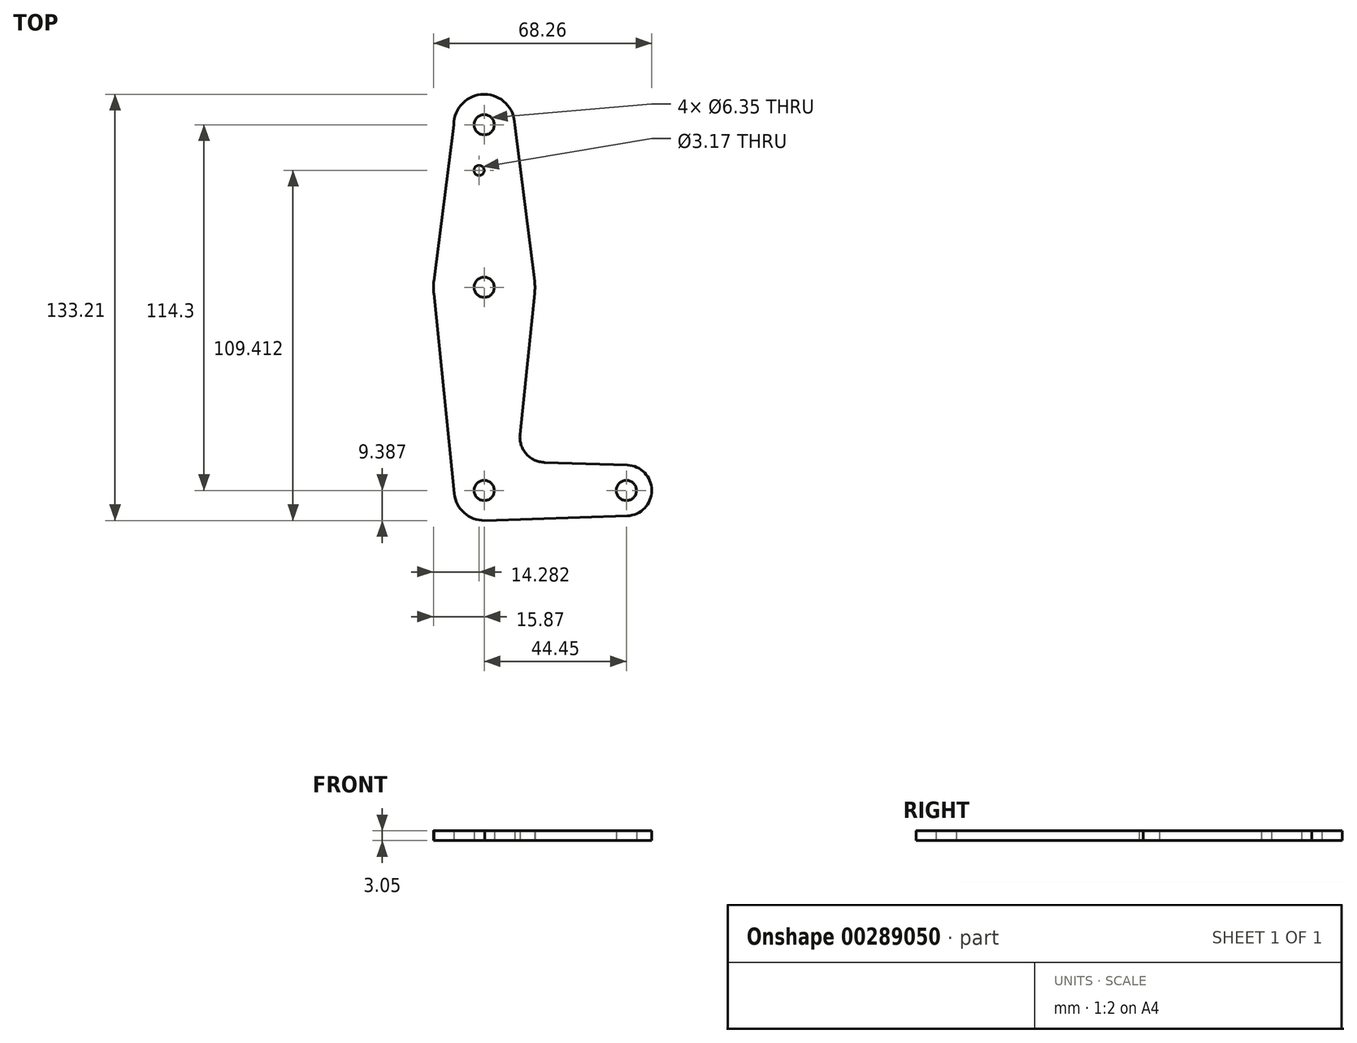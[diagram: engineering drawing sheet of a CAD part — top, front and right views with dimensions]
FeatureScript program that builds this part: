
annotation { "Feature Type Name" : "Feature", "Feature Type Description" : "" }
export const myFeature = defineFeature(function(context is Context, id is Id, definition is map)
    precondition{}
    {
        {
            var Q0;
            Q0=qCreatedBy(makeId("Top.planeOp"),FACE);
            var sketch = newSketch(context, id + "F0", { "sketchPlane" : qUnion([Q0])});
            skCircle(sketch, "E0", {"center": v(0, 37.39) * mm, "radius": 9.53 * mm});
            skCircle(sketch, "E1", {"center": v(0, -13.41) * mm, "radius": 15.88 * mm});
            skCircle(sketch, "E2", {"center": v(0, -76.91) * mm, "radius": 9.39 * mm});
            skCircle(sketch, "E3", {"center": v(44.45, -76.91) * mm, "radius": 7.94 * mm});
            skLineSegment(sketch, "E4", {"start": v(0, 37.39) * mm, "end": v(0, -76.91) * mm, "construction": true});
            skLineSegment(sketch, "E5", {"start": v(0, -76.91) * mm, "end": v(44.45, -76.91) * mm, "construction": true});
            skLineSegment(sketch, "E6", {"start": v(-9.52, 37.39) * mm, "end": v(-15.75, -11.4) * mm});
            skLineSegment(sketch, "E7", {"start": v(-15.75, -15.42) * mm, "end": v(-9.34, -77.87) * mm});
            skLineSegment(sketch, "E8", {"start": v(9.53, 37.39) * mm, "end": v(15.75, -11.4) * mm});
            skLineSegment(sketch, "E9", {"start": v(15.75, -15.42) * mm, "end": v(11.2, -59.38) * mm});
            skLineSegment(sketch, "E10", {"start": v(18.85, -68.14) * mm, "end": v(44.7, -68.98) * mm});
            skLineSegment(sketch, "E11", {"start": v(0.15, -86.3) * mm, "end": v(44.7, -84.85) * mm});
            skCircle(sketch, "E12", {"center": v(0, -76.91) * mm, "radius": 3.18 * mm});
            skCircle(sketch, "E13", {"center": v(44.45, -76.91) * mm, "radius": 3.18 * mm});
            skCircle(sketch, "E14", {"center": v(0, 37.39) * mm, "radius": 3.18 * mm});
            skArc(sketch, "E15.filletArc", {"start": v(11.2, -59.38) * mm, "mid": v(13.12, -65.42) * mm, "end": v(18.85, -68.14) * mm});
            skCircle(sketch, "E16", {"center": v(0, -13.41) * mm, "radius": 3.18 * mm});
            skCircle(sketch, "E17", {"center": v(-1.59, 23.11) * mm, "radius": 1.59 * mm});
            skSolve(sketch);
        }
        {
            var Q0;
            {var subQ1=sQuery(id+"F0.wireOp",EDGE,"E6");Q0=makeQuery(id+"F0.imprint","IMPRINT",FACE,{"disambiguationData":[TD([[makeQuery(id+"F0.imprint","IMPRINT",EDGE,{"derivedFrom":subQ1}),1.0]])]});}
            var Q1;
            Q1=makeQuery(id+"F0.imprint","IMPRINT",FACE,{"disambiguationData":[TD([[makeQuery(id+"F0.imprint","IMPRINT",EDGE,{"derivedFrom":sQuery(id+"F0.wireOp",EDGE,"E16")}),-1.0]])]});
            var Q2;
            {var subQ0=sQuery(id+"F0.wireOp",EDGE,"E7");Q2=makeQuery(id+"F0.imprint","IMPRINT",FACE,{"disambiguationData":[TD([[makeQuery(id+"F0.imprint","IMPRINT",EDGE,{"derivedFrom":subQ0}),1.0]])]});}
            var Q3;
            Q3=makeQuery(id+"F0.imprint","IMPRINT",FACE,{"disambiguationData":[TD([[makeQuery(id+"F0.imprint","IMPRINT",EDGE,{"derivedFrom":sQuery(id+"F0.wireOp",EDGE,"E13")}),-1.0]])]});
            var Q4;
            {var subQ0=sQuery(id+"F0.wireOp",EDGE,"E11");var subQ1=sQuery(id+"F0.wireOp",EDGE,"E2");var subQ2=makeQuery(id+"F0.imprint","INTERSECT",VERTEX,{"disambiguationData":[OD(0.0)],"derivedFrom":[subQ1,subQ0]});Q4=makeQuery(id+"F0.imprint","IMPRINT",FACE,{"disambiguationData":[TD([[makeQuery(id+"F0.imprint","IMPRINT",EDGE,{"disambiguationData":[TD([[subQ2,-1.0]])],"derivedFrom":subQ1}),1.0]])]});}
            var Q5;
            Q5=makeQuery(id+"F0.imprint","IMPRINT",FACE,{"disambiguationData":[TD([[makeQuery(id+"F0.imprint","IMPRINT",EDGE,{"derivedFrom":sQuery(id+"F0.wireOp",EDGE,"E13")}),-1.0]])]});
            var Q6;
            {var subQ0=sQuery(id+"F0.wireOp",EDGE,"E11");var subQ1=sQuery(id+"F0.wireOp",EDGE,"E2");var subQ2=makeQuery(id+"F0.imprint","INTERSECT",VERTEX,{"disambiguationData":[OD(0.0)],"derivedFrom":[subQ1,subQ0]});Q6=makeQuery(id+"F0.imprint","IMPRINT",FACE,{"disambiguationData":[TD([[makeQuery(id+"F0.imprint","IMPRINT",EDGE,{"disambiguationData":[TD([[subQ2,-1.0]])],"derivedFrom":subQ1}),1.0]])]});}
            var Q7;
            {var subQ1=sQuery(id+"F0.wireOp",EDGE,"E6");Q7=makeQuery(id+"F0.imprint","IMPRINT",FACE,{"disambiguationData":[TD([[makeQuery(id+"F0.imprint","IMPRINT",EDGE,{"derivedFrom":subQ1}),1.0]])]});}
            var Q8;
            Q8=makeQuery(id+"F0.imprint","IMPRINT",FACE,{"disambiguationData":[TD([[makeQuery(id+"F0.imprint","IMPRINT",EDGE,{"derivedFrom":sQuery(id+"F0.wireOp",EDGE,"E16")}),-1.0]])]});
            var Q9;
            {var subQ0=sQuery(id+"F0.wireOp",EDGE,"E7");Q9=makeQuery(id+"F0.imprint","IMPRINT",FACE,{"disambiguationData":[TD([[makeQuery(id+"F0.imprint","IMPRINT",EDGE,{"derivedFrom":subQ0}),1.0]])]});}
            var Q10;
            Q10=makeQuery(id+"F0.imprint","IMPRINT",FACE,{"disambiguationData":[TD([[makeQuery(id+"F0.imprint","IMPRINT",EDGE,{"derivedFrom":sQuery(id+"F0.wireOp",EDGE,"E14")}),-1.0]])]});
            var Q11;
            Q11=makeQuery(id+"F0.imprint","IMPRINT",FACE,{"disambiguationData":[TD([[makeQuery(id+"F0.imprint","IMPRINT",EDGE,{"derivedFrom":sQuery(id+"F0.wireOp",EDGE,"E12")}),-1.0]])]});
            extrude(context, id + "F1", {"entities" : qUnion([Q0, Q1, Q2, Q3, Q4, Q5, Q6, Q7, Q8, Q9, Q10, Q11]), "depth" : 3.05 * mm});
        }
    });
